# Revit family: 291 BFS-BEL-DSD-ME-Flash(LOD400)
name_source: partatom
category: Fire Alarm Devices
revit_build: Autodesk Revit 2018 (Build: 20170223_1515(x64)
units: mm (PartAtom-declared; Revit-internal decimal feet)

## family parameters
Cut with Voids When Loaded = No
Host = Face
Maintain Annotation Orientation = No
OmniClass Number = 23.29.31.15.11
OmniClass Title = Audible Fire Notification Devices Bell
Part Type = Normal
Room Calculation Point = No
Round Connector Dimension = Use Diameter
Shared = No

## types (1)
- 291 BFS-BEL-DSD-ME-Flash(LOD400)
    DSD.BFS.Height = 0 mm  [stored 0 ft]
    DSD.BFS.Length = 0 mm  [stored 0 ft]
    DSD.BFS.Width = 0 mm  [stored 0 ft]
    Default Elevation = 0 mm  [stored 0 ft]
    Depth = 73 mm
    Diameter = 200 mm  [stored 0.656168 ft]
    Glass_128255128 = GF_Glass_076-076-250
    Red_255000000 = ME_Red_255-000-000
    Silver_200200200 = ME_Silver_200-200-200
    White_255255255 = ME_White_255-255-255
    r/2 = 100 mm  [stored 0.328084 ft]

note: [stored X ft] marks values corroborated as IEEE doubles in the binary element streams (Revit-internal decimal feet)

## geometry (parser evidence)
native form markers: Sweep x17
no freeform markers — native parametric forms only
